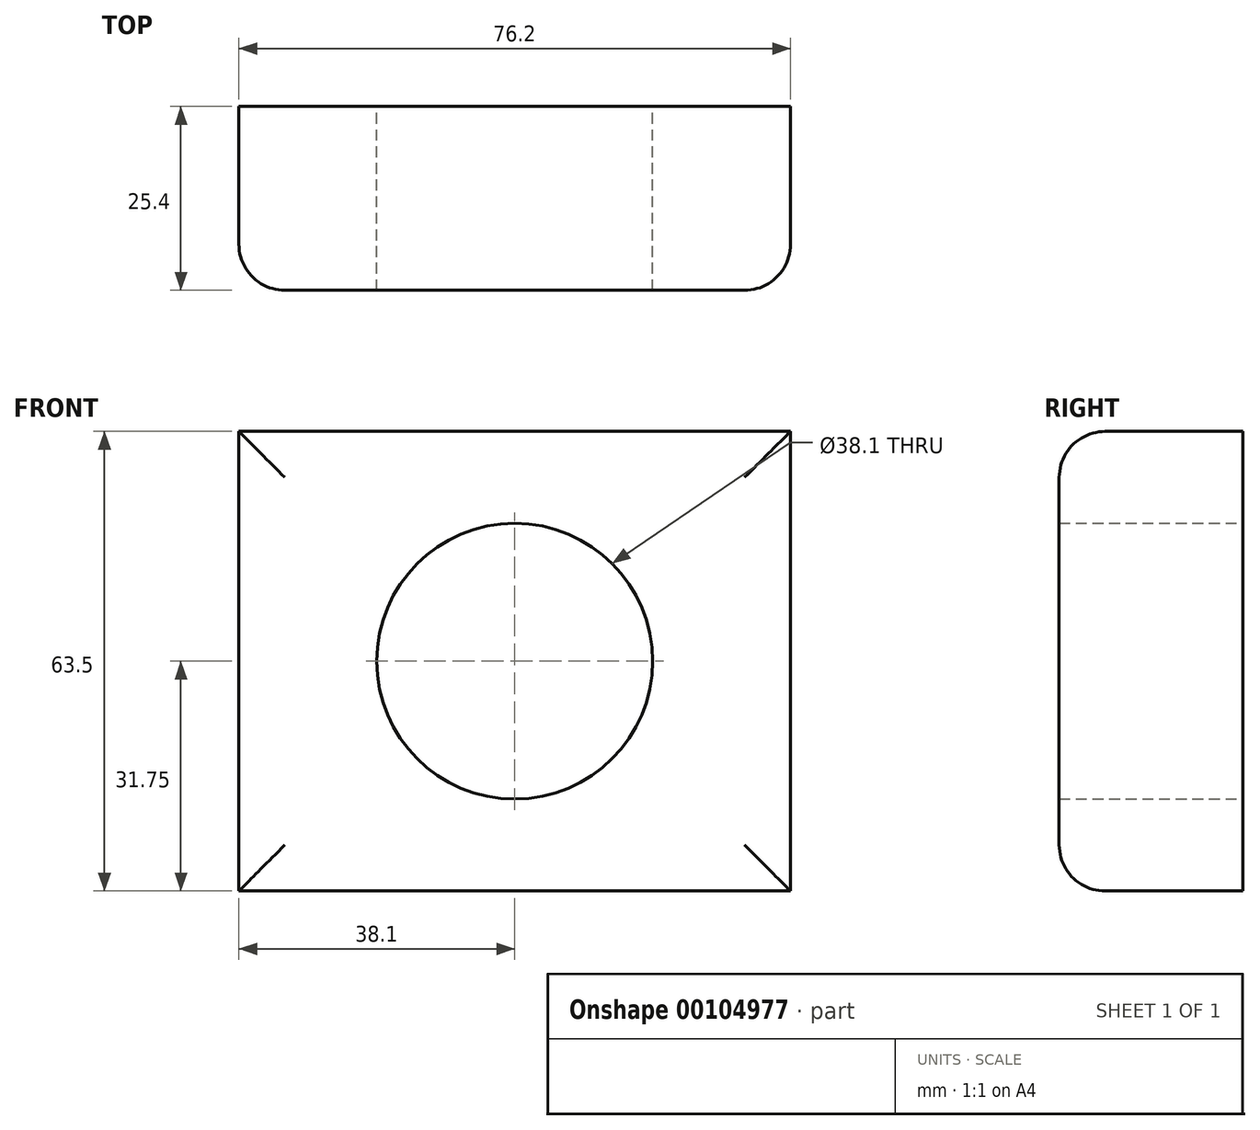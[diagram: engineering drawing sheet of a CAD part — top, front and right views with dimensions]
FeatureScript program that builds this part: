
annotation { "Feature Type Name" : "Feature", "Feature Type Description" : "" }
export const myFeature = defineFeature(function(context is Context, id is Id, definition is map)
    precondition{}
    {
        {
            var Q0;
            Q0=qCreatedBy(makeId("Front.planeOp"),FACE);
            var sketch = newSketch(context, id + "F0", { "sketchPlane" : qUnion([Q0])});
            skLineSegment(sketch, "E0", {"start": v(-38.1, 31.75) * mm, "end": v(-38.1, -31.75) * mm});
            skLineSegment(sketch, "E1", {"start": v(-38.1, -31.75) * mm, "end": v(38.1, -31.75) * mm});
            skLineSegment(sketch, "E2", {"start": v(38.1, -31.75) * mm, "end": v(38.1, 31.75) * mm});
            skLineSegment(sketch, "E3", {"start": v(38.1, 31.75) * mm, "end": v(-38.1, 31.75) * mm});
            skCircle(sketch, "E4", {"center": v(0, 0) * mm, "radius": 19.05 * mm});
            skSolve(sketch);
        }
        {
            var Q0;
            Q0=makeQuery(id+"F0.imprint","IMPRINT",FACE,{"disambiguationData":[TD([[makeQuery(id+"F0.imprint","IMPRINT",EDGE,{"derivedFrom":sQuery(id+"F0.wireOp",EDGE,"E0")}),1.0]])]});
            extrude(context, id + "F1", {"entities" : qUnion([Q0]), "endBound" : BoundingType.SYMMETRIC, "depth" : 25.4 * mm});
        }
        {
            var Q0;
            Q0=makeQuery(id+"F1.opExtrude","CAP_EDGE",EDGE,{"disambiguationData":[OSD([sQuery(id+"F0.wireOp",EDGE,"E2")])],"isStart":false});
            var Q1;
            Q1=makeQuery(id+"F1.opExtrude","CAP_EDGE",EDGE,{"disambiguationData":[OSD([sQuery(id+"F0.wireOp",EDGE,"E1")])],"isStart":false});
            var Q2;
            Q2=makeQuery(id+"F1.opExtrude","CAP_EDGE",EDGE,{"disambiguationData":[OSD([sQuery(id+"F0.wireOp",EDGE,"E0")])],"isStart":false});
            var Q3;
            Q3=makeQuery(id+"F1.opExtrude","CAP_EDGE",EDGE,{"disambiguationData":[OSD([sQuery(id+"F0.wireOp",EDGE,"E3")])],"isStart":false});
            fillet(context, id + "F2", {"entities" : qUnion([Q0, Q1, Q2, Q3]), "radius" : 6.35 * mm, "tangentPropagation" : true, "allowEdgeOverflow" : false});
        }
    });
